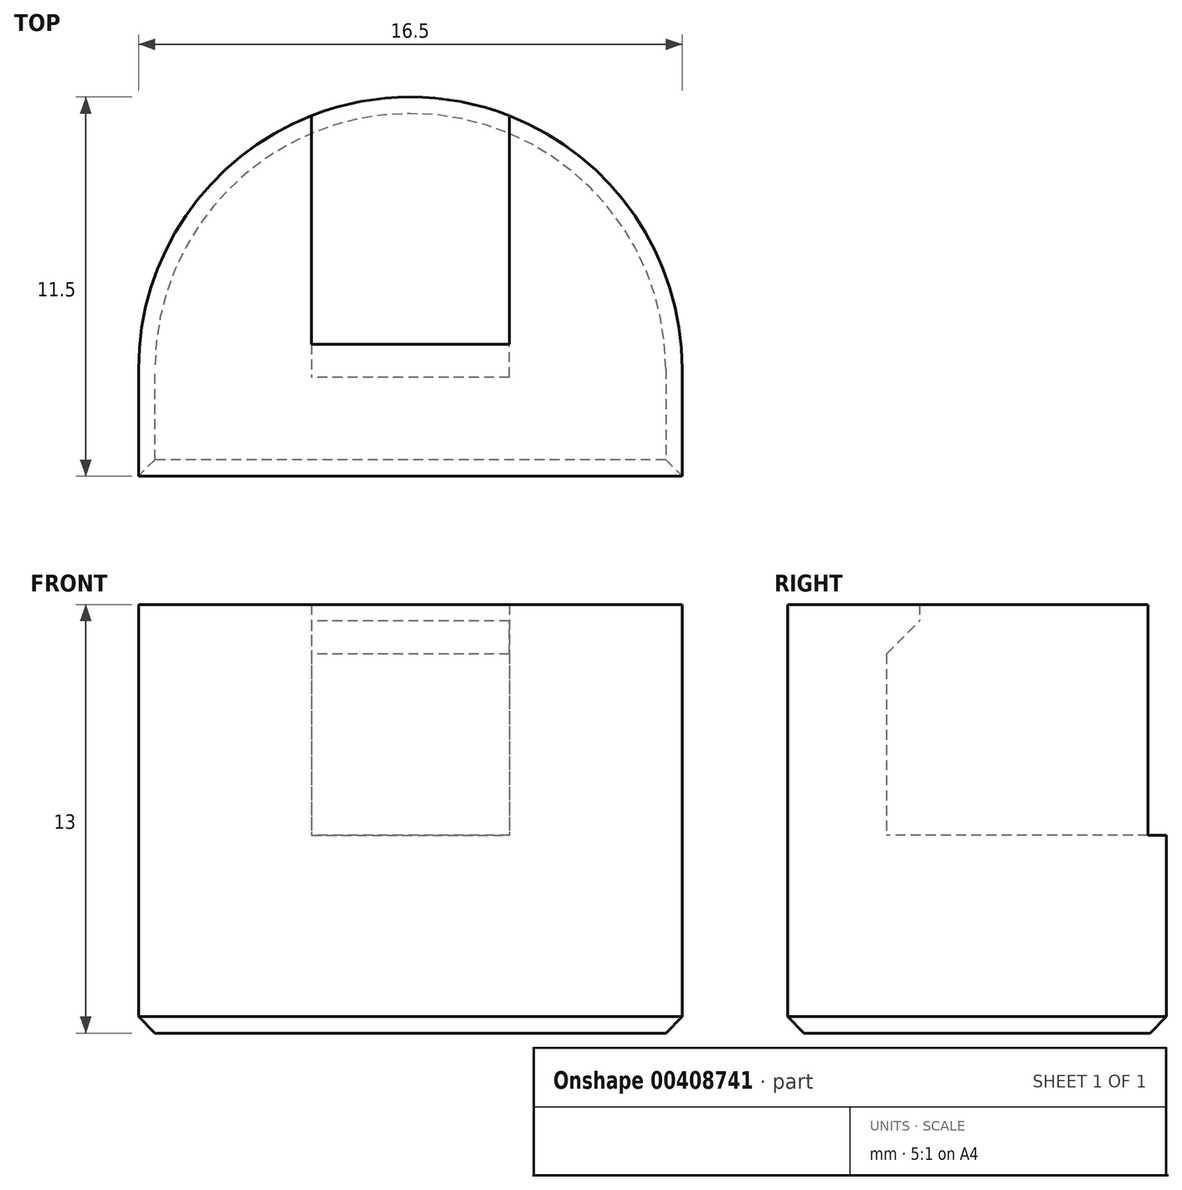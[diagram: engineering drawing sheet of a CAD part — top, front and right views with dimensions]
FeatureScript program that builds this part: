
annotation { "Feature Type Name" : "Feature", "Feature Type Description" : "" }
export const myFeature = defineFeature(function(context is Context, id is Id, definition is map)
    precondition{}
    {
        {
            assignVariable(context, id + "F0", {"name" : "hole_depth", "anyValue" : 10});
        }
        {
            assignVariable(context, id + "F1", {"name" : "insert_depth", "anyValue" : 5});
        }
        {
            assignVariable(context, id + "F2", {"name" : "extra_depth", "anyValue" : 2});
        }
        {
            var Q0;
            Q0=qCreatedBy(makeId("Top.planeOp"),FACE);
            var sketch = newSketch(context, id + "F3", { "sketchPlane" : qUnion([Q0])});
            skLineSegment(sketch, "E0", {"start": v(0, 0) * mm, "end": v(0, 11.5) * mm, "construction": true});
            skLineSegment(sketch, "E1", {"start": v(0, 0) * mm, "end": v(8.25, 0) * mm});
            skLineSegment(sketch, "E2", {"start": v(8.25, 0) * mm, "end": v(0, 0) * mm, "construction": true});
            skLineSegment(sketch, "E3", {"start": v(0, 0) * mm, "end": v(-8.25, 0) * mm, "construction": true});
            skLineSegment(sketch, "E4", {"start": v(-8.25, 0) * mm, "end": v(-8.25, 3.25) * mm});
            skLineSegment(sketch, "E5", {"start": v(8.25, 0) * mm, "end": v(8.25, 3.25) * mm});
            skArc(sketch, "E6", {"start": v(-8.25, 3.25) * mm, "mid": v(0, 11.5) * mm, "end": v(8.25, 3.25) * mm});
            skLineSegment(sketch, "E7", {"start": v(-8.25, 0) * mm, "end": v(8.25, 0) * mm});
            skSolve(sketch);
        }
        {
            var Q0;
            {var subQ0=sQuery(id+"F3.wireOp",EDGE,"E4");Q0=makeQuery(id+"F3.imprint","IMPRINT",FACE,{"disambiguationData":[TD([[makeQuery(id+"F3.imprint","IMPRINT",EDGE,{"derivedFrom":subQ0}),-1.0]])]});}
            extrude(context, id + "F4", {"entities" : qUnion([Q0]), "depth" : 1 * mm});
        }
        {
            var Q0;
            Q0=makeQuery(id+"F4.opExtrude","CAP_FACE",FACE,{"disambiguationData":[OSD([sQuery(id+"F3.wireOp",EDGE,"E4"),sQuery(id+"F3.wireOp",EDGE,"E5"),sQuery(id+"F3.wireOp",EDGE,"E6"),sQuery(id+"F3.wireOp",EDGE,"E7")])],"isStart":false});
            var sketch = newSketch(context, id + "F5", { "sketchPlane" : qUnion([Q0])});
            skPoint(sketch, "E8.middle", {"position": v(0, 0) * mm});
            skLineSegment(sketch, "E9.bottom", {"start": v(3, 12.5) * mm, "end": v(-3, 12.5) * mm});
            skLineSegment(sketch, "E9.top", {"start": v(3, -12.5) * mm, "end": v(-3, -12.5) * mm});
            skLineSegment(sketch, "E9.left", {"start": v(3, 12.5) * mm, "end": v(3, -12.5) * mm});
            skLineSegment(sketch, "E9.right", {"start": v(-3, 12.5) * mm, "end": v(-3, -12.5) * mm});
            skSolve(sketch);
        }
        {
            var Q0;
            {var subQ5=makeQuery(id+"F4.opExtrude","CAP_EDGE",EDGE,{"disambiguationData":[OSD([sQuery(id+"F3.wireOp",EDGE,"E4")])],"isStart":false});Q0=makeQuery(id+"F5.imprint","IMPRINT",FACE,{"disambiguationData":[TD([[makeQuery(id+"F5.imprint","IMPRINT",EDGE,{"derivedFrom":subQ5}),-1.0]])]});}
            var Q1;
            {var subQ5=makeQuery(id+"F4.opExtrude","CAP_EDGE",EDGE,{"disambiguationData":[OSD([sQuery(id+"F3.wireOp",EDGE,"E5")])],"isStart":false});Q1=makeQuery(id+"F5.imprint","IMPRINT",FACE,{"disambiguationData":[TD([[makeQuery(id+"F5.imprint","IMPRINT",EDGE,{"derivedFrom":subQ5}),1.0]])]});}
            extrude(context, id + "F6", {"entities" : qUnion([Q0, Q1]), "operationType" : NewBodyOperationType.ADD, "depth" : (getVariable(context, 'hole_depth') + getVariable(context, 'extra_depth')) * mm});
        }
        {
            var Q0;
            Q0=makeQuery(id+"F4.opExtrude","CAP_EDGE",EDGE,{"disambiguationData":[OSD([sQuery(id+"F3.wireOp",EDGE,"E5")])],"isStart":true});
            var Q1;
            Q1=makeQuery(id+"F4.opExtrude","CAP_EDGE",EDGE,{"disambiguationData":[OSD([sQuery(id+"F3.wireOp",EDGE,"E7")])],"isStart":true});
            chamfer(context, id + "F7", {"entities" : qUnion([Q0, Q1]), "width" : .5 * mm, "tangentPropagation" : true});
        }
        {
            var Q0;
            Q0=makeQuery(id+"F4.opExtrude","CAP_FACE",FACE,{"disambiguationData":[OSD([sQuery(id+"F3.wireOp",EDGE,"E4"),sQuery(id+"F3.wireOp",EDGE,"E5"),sQuery(id+"F3.wireOp",EDGE,"E6"),sQuery(id+"F3.wireOp",EDGE,"E7")])],"isStart":false});
            var sketch = newSketch(context, id + "F8", { "sketchPlane" : qUnion([Q0])});
            skLineSegment(sketch, "E10.bottom", {"start": v(-3, 0) * mm, "end": v(3, 0) * mm});
            skLineSegment(sketch, "E10.top", {"start": v(-3, 3) * mm, "end": v(3, 3) * mm});
            skLineSegment(sketch, "E10.left", {"start": v(-3, 0) * mm, "end": v(-3, 3) * mm});
            skLineSegment(sketch, "E10.right", {"start": v(3, 0) * mm, "end": v(3, 3) * mm});
            skSolve(sketch);
        }
        {
            var Q0;
            Q0=makeQuery(id+"F8.imprint","IMPRINT",FACE,{"disambiguationData":[TD([[makeQuery(id+"F8.imprint","IMPRINT",EDGE,{"derivedFrom":sQuery(id+"F8.wireOp",EDGE,"E10.bottom")}),1.0]])]});
            extrude(context, id + "F9", {"entities" : qUnion([Q0]), "operationType" : NewBodyOperationType.ADD, "depth" : (getVariable(context, 'hole_depth') + getVariable(context, 'extra_depth')) * mm});
        }
        {
            var Q0;
            Q0=makeQuery(id+"F4.opExtrude","CAP_FACE",FACE,{"disambiguationData":[OSD([sQuery(id+"F3.wireOp",EDGE,"E4"),sQuery(id+"F3.wireOp",EDGE,"E5"),sQuery(id+"F3.wireOp",EDGE,"E6"),sQuery(id+"F3.wireOp",EDGE,"E7")])],"isStart":false});
            extrude(context, id + "F10", {"entities" : qUnion([Q0]), "operationType" : NewBodyOperationType.ADD, "depth" : (getVariable(context, 'hole_depth') - getVariable(context, 'insert_depth')) * mm});
        }
        {
            var Q0;
            Q0=makeQuery(id+"F9.opExtrude","SWEPT_FACE",FACE,{"disambiguationData":[OSD([sQuery(id+"F8.wireOp",EDGE,"E10.top")])]});
            var sketch = newSketch(context, id + "F11", { "sketchPlane" : qUnion([Q0])});
            skLineSegment(sketch, "E11.bottom", {"start": v(-3, 13) * mm, "end": v(3, 13) * mm});
            skLineSegment(sketch, "E11.top", {"start": v(-3, 11.5) * mm, "end": v(3, 11.5) * mm});
            skLineSegment(sketch, "E11.left", {"start": v(-3, 13) * mm, "end": v(-3, 11.5) * mm});
            skLineSegment(sketch, "E11.right", {"start": v(3, 13) * mm, "end": v(3, 11.5) * mm});
            skSolve(sketch);
        }
        {
            var Q0;
            Q0=makeQuery(id+"F11.imprint","IMPRINT",FACE,{"disambiguationData":[TD([[makeQuery(id+"F11.imprint","IMPRINT",EDGE,{"derivedFrom":sQuery(id+"F11.wireOp",EDGE,"E11.bottom")}),1.0]])]});
            extrude(context, id + "F12", {"entities" : qUnion([Q0]), "operationType" : NewBodyOperationType.ADD, "depth" : 1 * mm});
        }
        {
            var Q0;
            Q0=makeQuery(id+"F12.opExtrude","CAP_EDGE",EDGE,{"disambiguationData":[OSD([sQuery(id+"F11.wireOp",EDGE,"E11.top")])],"isStart":false});
            chamfer(context, id + "F13", {"entities" : qUnion([Q0]), "width" : 1 * mm, "tangentPropagation" : true});
        }
    });
